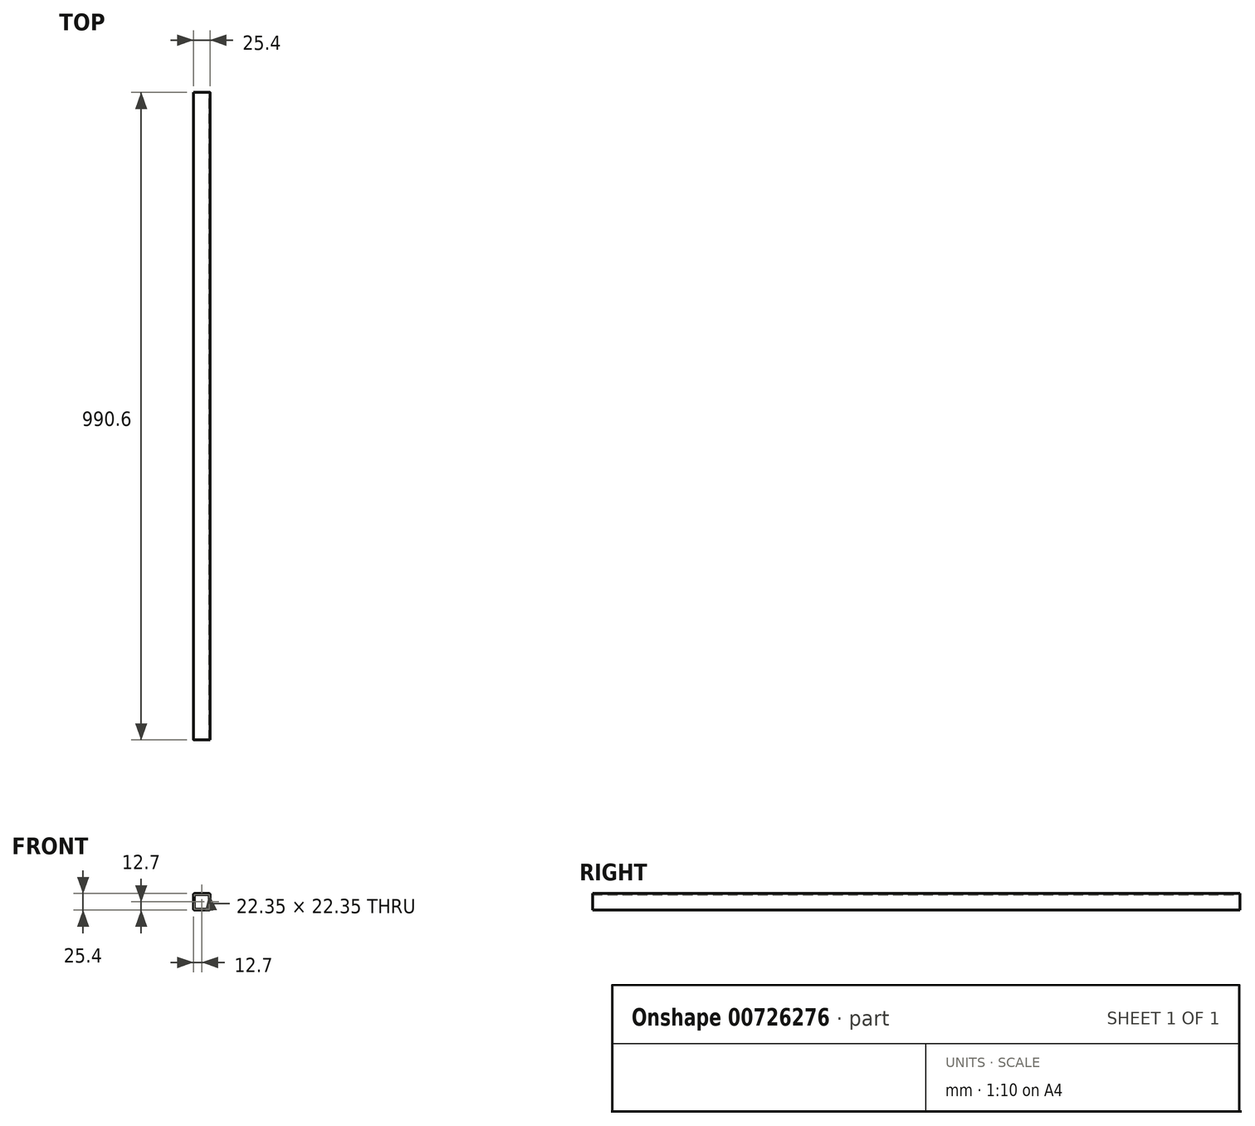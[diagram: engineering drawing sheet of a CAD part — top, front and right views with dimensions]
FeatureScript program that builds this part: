
annotation { "Feature Type Name" : "Feature", "Feature Type Description" : "" }
export const myFeature = defineFeature(function(context is Context, id is Id, definition is map)
    precondition{}
    {
        {
            var Q0;
            Q0=qCreatedBy(makeId("Front.planeOp"),FACE);
            var sketch = newSketch(context, id + "F0", { "sketchPlane" : qUnion([Q0])});
            skLineSegment(sketch, "E0.bottom", {"start": v(1.52, 0) * mm, "end": v(23.88, 0) * mm});
            skLineSegment(sketch, "E0.top", {"start": v(1.52, 25.4) * mm, "end": v(23.88, 25.4) * mm});
            skLineSegment(sketch, "E0.left", {"start": v(0, 1.52) * mm, "end": v(0, 23.88) * mm});
            skLineSegment(sketch, "E0.right", {"start": v(25.4, 1.52) * mm, "end": v(25.4, 23.88) * mm});
            skPoint(sketch, "E1.visualSharp", {"position": v(0, 25.4) * mm});
            skArc(sketch, "E1.filletArc", {"start": v(1.52, 25.4) * mm, "mid": v(0.45, 24.95) * mm, "end": v(0, 23.88) * mm});
            skPoint(sketch, "E2.visualSharp", {"position": v(25.4, 25.4) * mm});
            skArc(sketch, "E2.filletArc", {"start": v(25.4, 23.88) * mm, "mid": v(24.95, 24.95) * mm, "end": v(23.88, 25.4) * mm});
            skPoint(sketch, "E3.visualSharp", {"position": v(25.4, 0) * mm});
            skArc(sketch, "E3.filletArc", {"start": v(23.88, 0) * mm, "mid": v(24.95, 0.45) * mm, "end": v(25.4, 1.52) * mm});
            skPoint(sketch, "E4.visualSharp", {"position": v(0, 0) * mm});
            skArc(sketch, "E4.filletArc", {"start": v(0, 1.52) * mm, "mid": v(0.45, 0.45) * mm, "end": v(1.52, 0) * mm});
            skLineSegment(sketch, "E5.0", {"start": v(1.52, 23.88) * mm, "end": v(23.88, 23.88) * mm});
            skLineSegment(sketch, "E6.0", {"start": v(23.88, 23.88) * mm, "end": v(23.88, 23.88) * mm});
            skLineSegment(sketch, "E6.1", {"start": v(23.88, 1.52) * mm, "end": v(23.88, 23.88) * mm});
            skLineSegment(sketch, "E6.2", {"start": v(23.88, 1.52) * mm, "end": v(23.88, 1.52) * mm});
            skLineSegment(sketch, "E6.3", {"start": v(1.52, 23.88) * mm, "end": v(1.52, 23.88) * mm});
            skLineSegment(sketch, "E6.4", {"start": v(1.52, 1.52) * mm, "end": v(1.52, 23.88) * mm});
            skLineSegment(sketch, "E6.5", {"start": v(1.52, 1.52) * mm, "end": v(1.52, 1.52) * mm});
            skLineSegment(sketch, "E6.6", {"start": v(1.52, 1.52) * mm, "end": v(23.88, 1.52) * mm});
            skSolve(sketch);
        }
        {
            var Q0;
            Q0 = qSketchRegion(id + "F0", true);
            extrude(context, id + "F1", {"entities" : qUnion([Q0]), "depth" : 990.6 * mm, "offsetDistance" : 25.4 * mm});
        }
    });
